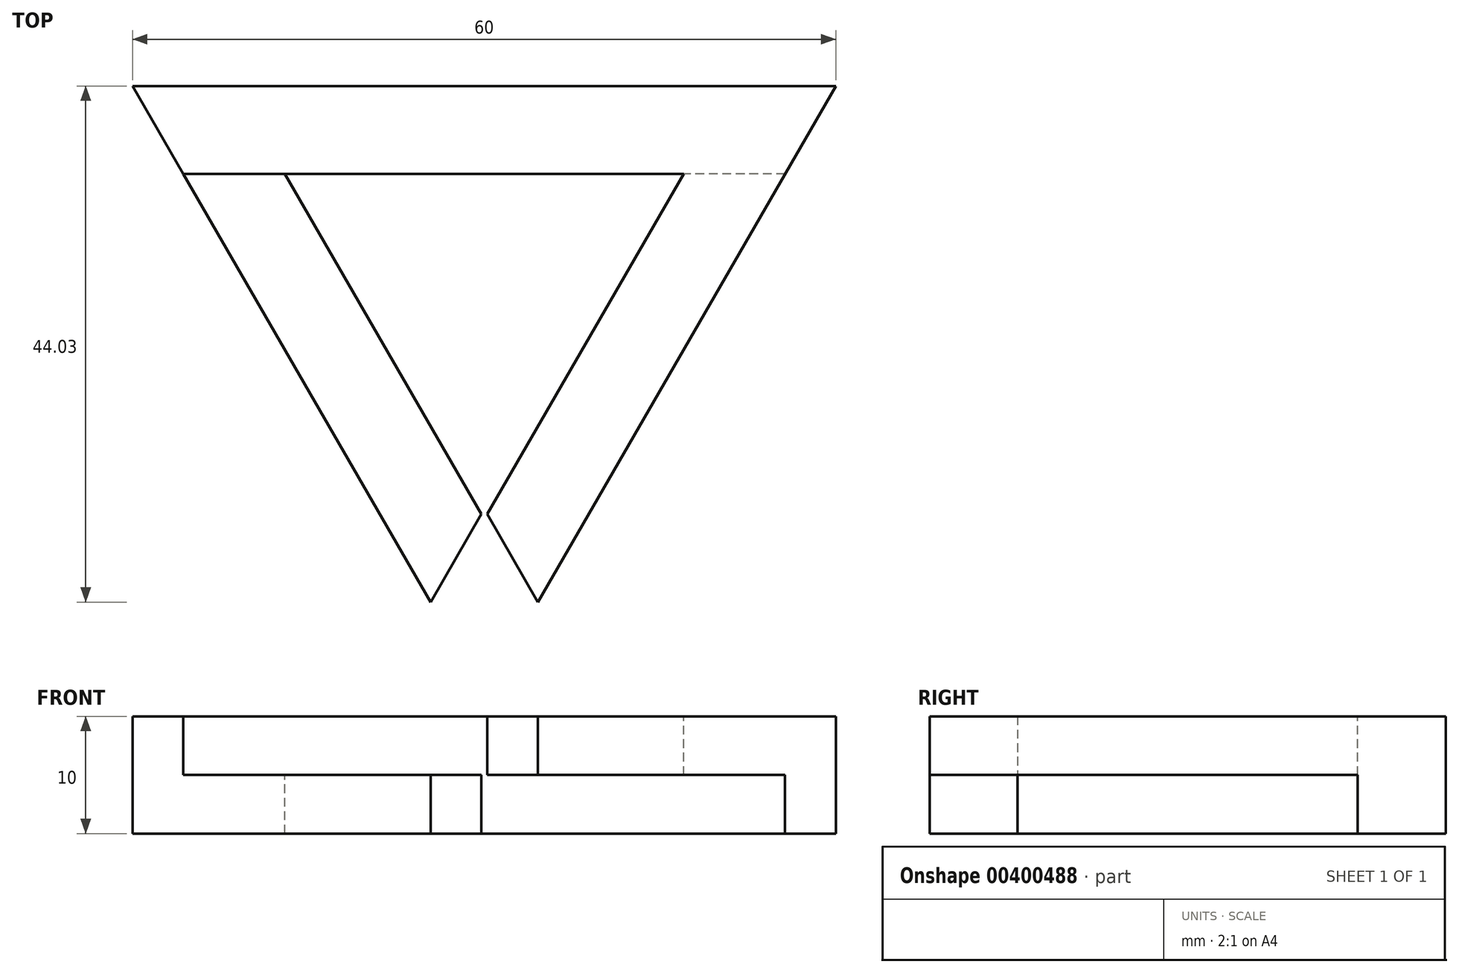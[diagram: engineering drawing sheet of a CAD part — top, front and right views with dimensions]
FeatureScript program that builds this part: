
annotation { "Feature Type Name" : "Feature", "Feature Type Description" : "" }
export const myFeature = defineFeature(function(context is Context, id is Id, definition is map)
    precondition{}
    {
        {
            var Q0;
            Q0=qCreatedBy(makeId("Top.planeOp"),FACE);
            var sketch = newSketch(context, id + "F0", { "sketchPlane" : qUnion([Q0])});
            skCircle(sketch, "E0.cCircle", {"center": v(0, 0) * mm, "radius": 17.32 * mm, "construction": true});
            skLineSegment(sketch, "E0.0", {"start": v(-30, 17.32) * mm, "end": v(30, 17.32) * mm});
            skLineSegment(sketch, "E0.1", {"start": v(30, 17.32) * mm, "end": v(0, -34.64) * mm});
            skLineSegment(sketch, "E0.2", {"start": v(0, -34.64) * mm, "end": v(-30, 17.32) * mm});
            skPoint(sketch, "E0.0.midPoint", {"position": v(0, 17.32) * mm});
            skSolve(sketch);
        }
        {
            var Q0;
            Q0 = qSketchRegion(id + "F0", true);
            extrude(context, id + "F1", {"entities" : qUnion([Q0]), "depth" : 10 * mm});
        }
        {
            var Q0;
            Q0=makeQuery(id+"F1.opExtrude","CAP_FACE",FACE,{"disambiguationData":[OSD([sQuery(id+"F0.wireOp",EDGE,"E0.0"),sQuery(id+"F0.wireOp",EDGE,"E0.1"),sQuery(id+"F0.wireOp",EDGE,"E0.2")])],"isStart":false});
            var sketch = newSketch(context, id + "F2", { "sketchPlane" : qUnion([Q0])});
            skCircle(sketch, "E1.cCircle", {"center": v(0, 0) * mm, "radius": 9.82 * mm, "construction": true});
            skLineSegment(sketch, "E1.0", {"start": v(-17, 9.82) * mm, "end": v(17, 9.82) * mm});
            skLineSegment(sketch, "E1.1", {"start": v(17, 9.82) * mm, "end": v(0, -19.64) * mm});
            skLineSegment(sketch, "E1.2", {"start": v(0, -19.64) * mm, "end": v(-17, 9.82) * mm});
            skPoint(sketch, "E1.0.midPoint", {"position": v(0, 9.82) * mm});
            skSolve(sketch);
        }
        {
            var Q0;
            Q0 = qSketchRegion(id + "F2", true);
            extrude(context, id + "F3", {"entities" : qUnion([Q0]), "operationType" : NewBodyOperationType.REMOVE, "endBound" : BoundingType.THROUGH_ALL, "oppositeDirection" : true, "depth" : 25 * mm});
        }
        {
            var Q0;
            Q0=makeQuery(id+"F1.opExtrude","CAP_FACE",FACE,{"disambiguationData":[OSD([sQuery(id+"F0.wireOp",EDGE,"E0.0"),sQuery(id+"F0.wireOp",EDGE,"E0.1"),sQuery(id+"F0.wireOp",EDGE,"E0.2")])],"isStart":true});
            var sketch = newSketch(context, id + "F4", { "sketchPlane" : qUnion([Q0])});
            skLineSegment(sketch, "E2", {"start": v(0, 19.64) * mm, "end": v(0, 34.64) * mm});
            skLineSegment(sketch, "E3", {"start": v(0, 34.64) * mm, "end": v(25.67, -9.82) * mm});
            skLineSegment(sketch, "E4", {"start": v(25.67, -9.82) * mm, "end": v(17, -9.82) * mm});
            skLineSegment(sketch, "E5", {"start": v(17, -9.82) * mm, "end": v(0, 19.64) * mm});
            skLineSegment(sketch, "E6", {"start": v(-25.67, -9.82) * mm, "end": v(-17, -9.82) * mm});
            skLineSegment(sketch, "E7", {"start": v(-17, -9.82) * mm, "end": v(0, 19.64) * mm});
            skSolve(sketch);
        }
        {
            var Q0;
            Q0=makeQuery(id+"F1.opExtrude","CAP_FACE",FACE,{"disambiguationData":[OSD([sQuery(id+"F0.wireOp",EDGE,"E0.0"),sQuery(id+"F0.wireOp",EDGE,"E0.1"),sQuery(id+"F0.wireOp",EDGE,"E0.2")])],"isStart":false});
            var sketch = newSketch(context, id + "F5", { "sketchPlane" : qUnion([Q0])});
            skLineSegment(sketch, "E8", {"start": v(0, -19.64) * mm, "end": v(0, -34.64) * mm});
            skLineSegment(sketch, "E9", {"start": v(0, -34.64) * mm, "end": v(-25.67, 9.82) * mm});
            skLineSegment(sketch, "E10", {"start": v(-25.67, 9.82) * mm, "end": v(-17, 9.82) * mm});
            skLineSegment(sketch, "E11", {"start": v(-17, 9.82) * mm, "end": v(0, -19.64) * mm});
            skSolve(sketch);
        }
        {
            var Q0;
            Q0=makeQuery(id+"F1.opExtrude","CAP_FACE",FACE,{"disambiguationData":[OSD([sQuery(id+"F0.wireOp",EDGE,"E0.0"),sQuery(id+"F0.wireOp",EDGE,"E0.1"),sQuery(id+"F0.wireOp",EDGE,"E0.2")])],"isStart":true});
            var sketch = newSketch(context, id + "F6", { "sketchPlane" : qUnion([Q0])});
            skLineSegment(sketch, "E12", {"start": v(0, 34.64) * mm, "end": v(0, 19.64) * mm});
            skPoint(sketch, "E13.endSnap0", {"position": v(0, 27.14) * mm});
            skLineSegment(sketch, "E14", {"start": v(4.33, 27.14) * mm, "end": v(0, 34.64) * mm});
            skLineSegment(sketch, "E15", {"start": v(0, 34.64) * mm, "end": v(-4.33, 27.14) * mm});
            skLineSegment(sketch, "E16", {"start": v(0, 19.64) * mm, "end": v(-0.25, 19.2) * mm});
            skLineSegment(sketch, "E17", {"start": v(-0.25, 19.2) * mm, "end": v(0.25, 19.2) * mm});
            skLineSegment(sketch, "E18", {"start": v(0.25, 19.2) * mm, "end": v(0, 19.64) * mm});
            skLineSegment(sketch, "E19", {"start": v(0.25, 19.2) * mm, "end": v(4.58, 26.7) * mm});
            skLineSegment(sketch, "E20", {"start": v(4.58, 26.7) * mm, "end": v(4.33, 27.14) * mm});
            skLineSegment(sketch, "E21", {"start": v(-0.25, 19.2) * mm, "end": v(-4.58, 26.7) * mm});
            skLineSegment(sketch, "E22", {"start": v(-4.58, 26.7) * mm, "end": v(-4.33, 27.14) * mm});
            skSolve(sketch);
        }
        {
            var Q0;
            Q0 = qSketchRegion(id + "F6", true);
            extrude(context, id + "F7", {"entities" : qUnion([Q0]), "operationType" : NewBodyOperationType.REMOVE, "endBound" : BoundingType.THROUGH_ALL, "oppositeDirection" : true, "depth" : 25 * mm});
        }
        {
            var Q0;
            Q0 = qSketchRegion(id + "F6", true);
            extrude(context, id + "F8", {"entities" : qUnion([Q0]), "operationType" : NewBodyOperationType.REMOVE, "endBound" : BoundingType.THROUGH_ALL, "oppositeDirection" : true, "depth" : 25 * mm});
        }
        {
            var Q0;
            Q0 = qSketchRegion(id + "F5", true);
            extrude(context, id + "F9", {"entities" : qUnion([Q0]), "operationType" : NewBodyOperationType.REMOVE, "oppositeDirection" : true, "depth" : 5 * mm});
        }
        {
            var Q0;
            Q0 = qSketchRegion(id + "F4", true);
            extrude(context, id + "F10", {"entities" : qUnion([Q0]), "operationType" : NewBodyOperationType.REMOVE, "oppositeDirection" : true, "depth" : 5 * mm});
        }
    });
